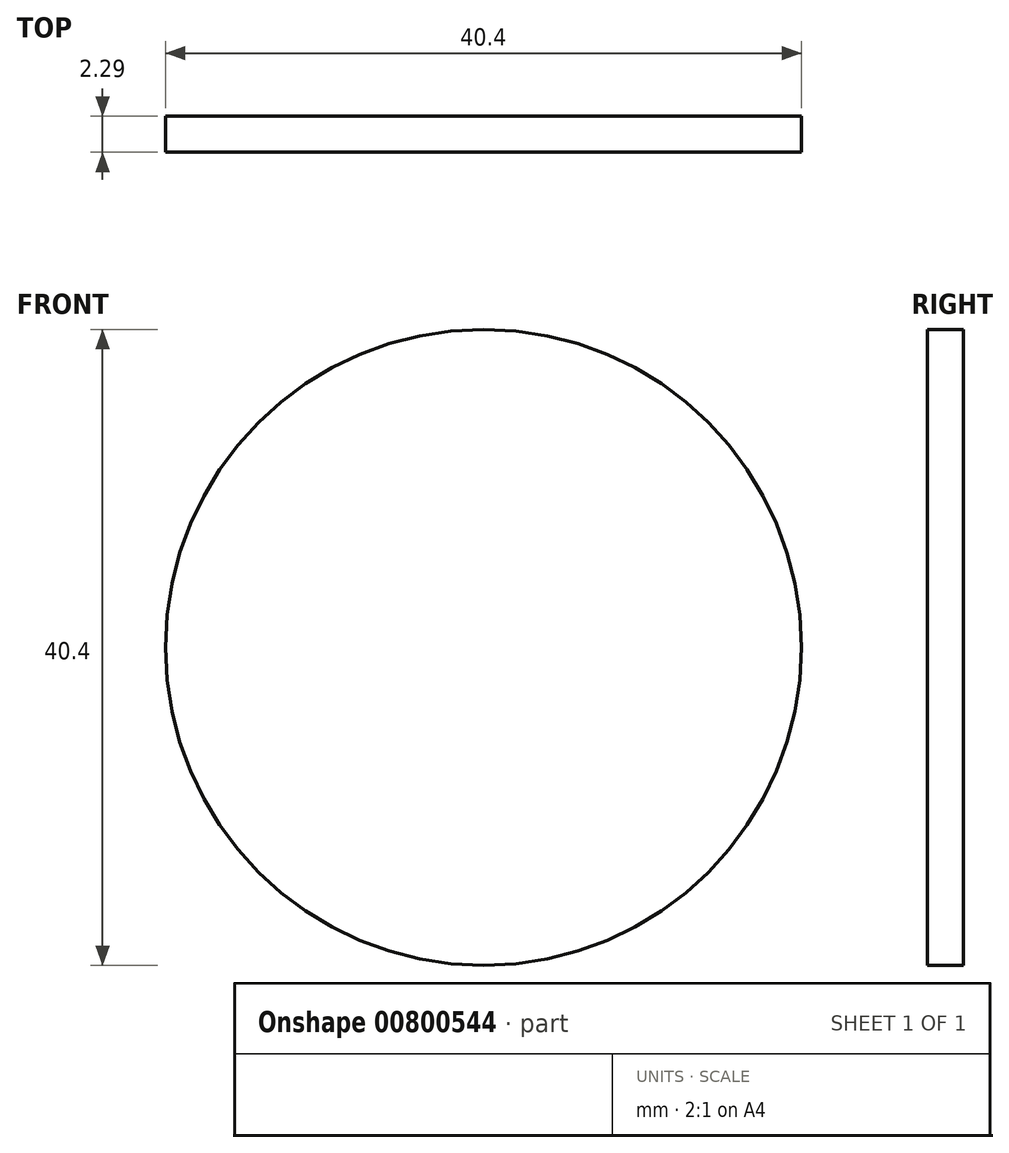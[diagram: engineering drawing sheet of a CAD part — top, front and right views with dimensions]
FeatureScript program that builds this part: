
annotation { "Feature Type Name" : "Feature", "Feature Type Description" : "" }
export const myFeature = defineFeature(function(context is Context, id is Id, definition is map)
    precondition{}
    {
        {
            var Q0;
            Q0=qCreatedBy(makeId("Front.planeOp"),FACE);
            var sketch = newSketch(context, id + "F0", { "sketchPlane" : qUnion([Q0])});
            skCircle(sketch, "E0", {"center": v(0, 0) * mm, "radius": 20.2 * mm});
            skSolve(sketch);
        }
        {
            var Q0;
            Q0=makeQuery(id+"F0.imprint","IMPRINT",FACE,{"disambiguationData":[TD([[makeQuery(id+"F0.imprint","IMPRINT",EDGE,{"derivedFrom":sQuery(id+"F0.wireOp",EDGE,"E0")}),1.0]])]});
            extrude(context, id + "F1", {"entities" : qUnion([Q0]), "oppositeDirection" : true, "depth" : 2.3 * mm, "offsetDistance" : 25.4 * mm});
        }
    });
